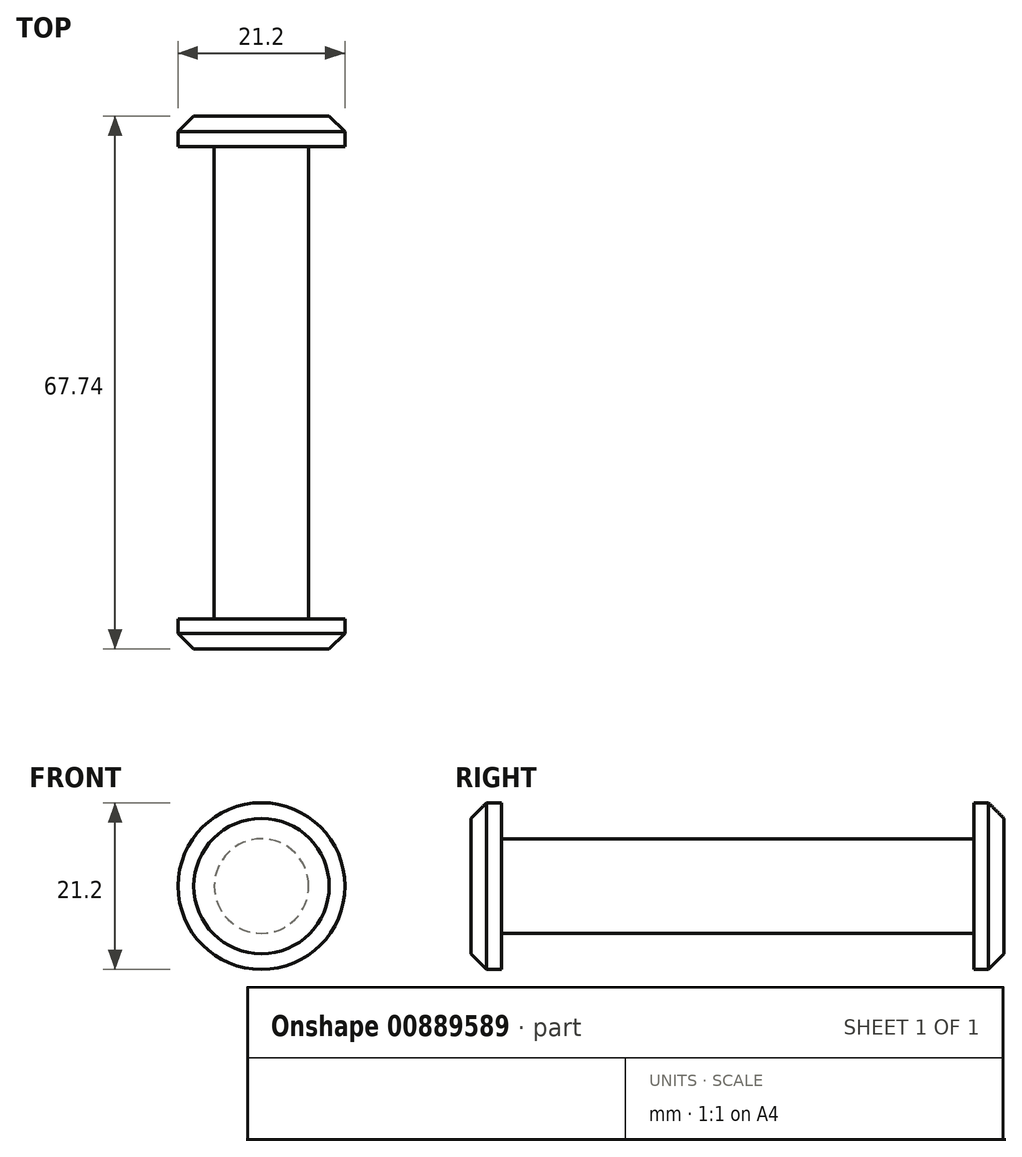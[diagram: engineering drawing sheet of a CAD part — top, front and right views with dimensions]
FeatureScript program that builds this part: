
annotation { "Feature Type Name" : "Feature", "Feature Type Description" : "" }
export const myFeature = defineFeature(function(context is Context, id is Id, definition is map)
    precondition{}
    {
        {
            var Q0;
            Q0=qCreatedBy(makeId("Right.planeOp"),FACE);
            var sketch = newSketch(context, id + "F0", { "sketchPlane" : qUnion([Q0])});
            skLineSegment(sketch, "E0", {"start": v(-33.87, 0) * mm, "end": v(-33.87, 10.6) * mm});
            skLineSegment(sketch, "E1", {"start": v(-33.87, 10.6) * mm, "end": v(-30, 10.6) * mm});
            skLineSegment(sketch, "E2", {"start": v(-30, 10.6) * mm, "end": v(-30, 6) * mm});
            skLineSegment(sketch, "E3", {"start": v(-30, 6) * mm, "end": v(0, 6) * mm});
            skLineSegment(sketch, "E4", {"start": v(0, 0) * mm, "end": v(-33.87, 0) * mm});
            skLineSegment(sketch, "E5.MirrorCS", {"start": v(33.87, 10.6) * mm, "end": v(30, 10.6) * mm});
            skLineSegment(sketch, "E6.MirrorCS", {"start": v(0, 0) * mm, "end": v(33.87, 0) * mm});
            skLineSegment(sketch, "E7.MirrorCS", {"start": v(33.87, 0) * mm, "end": v(33.87, 10.6) * mm});
            skLineSegment(sketch, "E8.MirrorCS", {"start": v(30, 10.6) * mm, "end": v(30, 6) * mm});
            skLineSegment(sketch, "E9.MirrorCS", {"start": v(30, 6) * mm, "end": v(0, 6) * mm});
            skSolve(sketch);
        }
        {
            var Q0;
            Q0=makeQuery(id+"F0.imprint","IMPRINT",FACE,{"disambiguationData":[TD([[makeQuery(id+"F0.imprint","IMPRINT",EDGE,{"derivedFrom":sQuery(id+"F0.wireOp",EDGE,"E0")}),-1.0]])]});
            var Q1;
            Q1=sQuery(id+"F0.wireOp",EDGE,"E4");
            revolve(context, id + "F1", {"surfaceOperationType" : NewSurfaceOperationType.NEW, "entities" : qUnion([Q0]), "axis" : qUnion([Q1]), "revolveType" : RevolveType.FULL});
        }
        {
            var Q0;
            Q0=makeQuery(id+"F1.opRevolve","SWEPT_EDGE",EDGE,{"disambiguationData":[OSD([sQuery(id+"F0.wireOp",EDGE,"E0"),sQuery(id+"F0.wireOp",EDGE,"E1")])]});
            var Q1;
            Q1=makeQuery(id+"F1.opRevolve","SWEPT_EDGE",EDGE,{"disambiguationData":[OSD([sQuery(id+"F0.wireOp",EDGE,"E5.MirrorCS"),sQuery(id+"F0.wireOp",EDGE,"E7.MirrorCS")])]});
            chamfer(context, id + "F2", {"entities" : qUnion([Q0, Q1]), "width" : 2 * mm, "tangentPropagation" : true});
        }
    });
